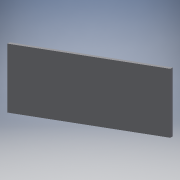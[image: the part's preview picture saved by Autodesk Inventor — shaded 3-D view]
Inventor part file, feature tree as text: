
AUTODESK INVENTOR PART (.ipt)
format: ipt  version: 2018.3 (Build 223284000, 284)  size: 84,992 bytes
history: native  units: mm
features: extrude x1, sketch x1
ambient origin geometry x8: Origin, YZ Plane, XZ Plane, XY Plane, X Axis, Y Axis, Z Axis, Center Point
bodies: Solid1 (feature_tree)
feature tree (2):
  extrude  "Extrusion1"  Depth=94.68479mm
  sketch  "Sketch1"  dims[d0=2.0mm d1=94.68479mm d2=30.0deg d3=2.0mm d4=50.0mm d5=0.0mm]
